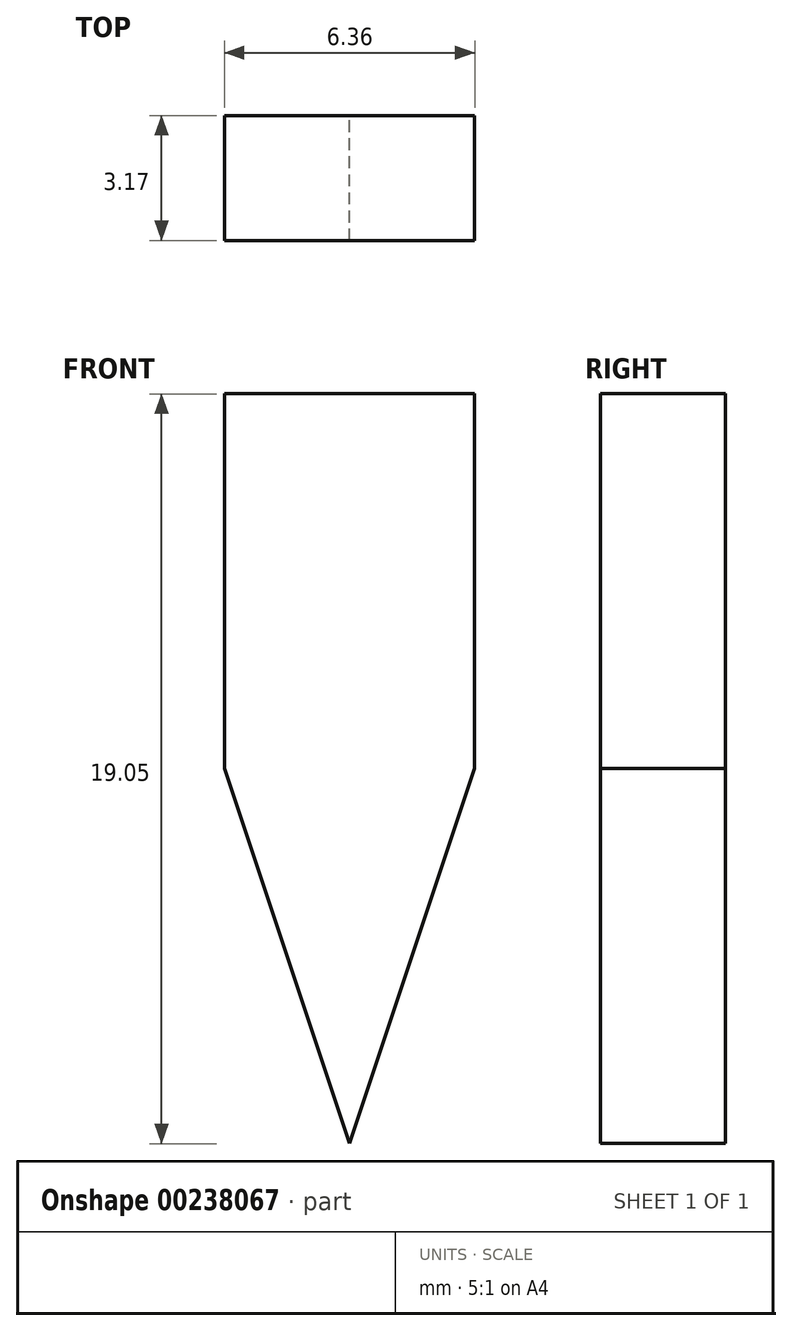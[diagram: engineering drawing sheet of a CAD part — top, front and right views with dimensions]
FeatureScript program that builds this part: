
annotation { "Feature Type Name" : "Feature", "Feature Type Description" : "" }
export const myFeature = defineFeature(function(context is Context, id is Id, definition is map)
    precondition{}
    {
        {
            var Q0;
            Q0=qCreatedBy(makeId("Front.planeOp"),FACE);
            var sketch = newSketch(context, id + "F0", { "sketchPlane" : qUnion([Q0])});
            skLineSegment(sketch, "E0.bottom", {"start": v(3.18, -4.76) * mm, "end": v(-3.18, -4.76) * mm});
            skLineSegment(sketch, "E0.top", {"start": v(3.18, 4.76) * mm, "end": v(-3.17, 4.76) * mm});
            skLineSegment(sketch, "E0.left", {"start": v(3.18, -4.76) * mm, "end": v(3.18, 4.76) * mm});
            skLineSegment(sketch, "E0.right", {"start": v(-3.18, -4.76) * mm, "end": v(-3.17, 4.76) * mm});
            skPoint(sketch, "E0.middle", {"position": v(0, 0) * mm});
            skLineSegment(sketch, "E1.0", {"start": v(3.17, -4.76) * mm, "end": v(0, -14.29) * mm});
            skLineSegment(sketch, "E1.1", {"start": v(0, -14.29) * mm, "end": v(-3.17, -4.76) * mm});
            skLineSegment(sketch, "E1.2", {"start": v(-3.18, -4.76) * mm, "end": v(3.17, -4.76) * mm});
            skPoint(sketch, "E1.0.midPoint", {"position": v(1.59, -9.53) * mm});
            skSolve(sketch);
        }
        {
            var Q0;
            Q0 = qSketchRegion(id + "F0", true);
            extrude(context, id + "F1", {"entities" : qUnion([Q0]), "depth" : 3.17 * mm});
        }
    });
